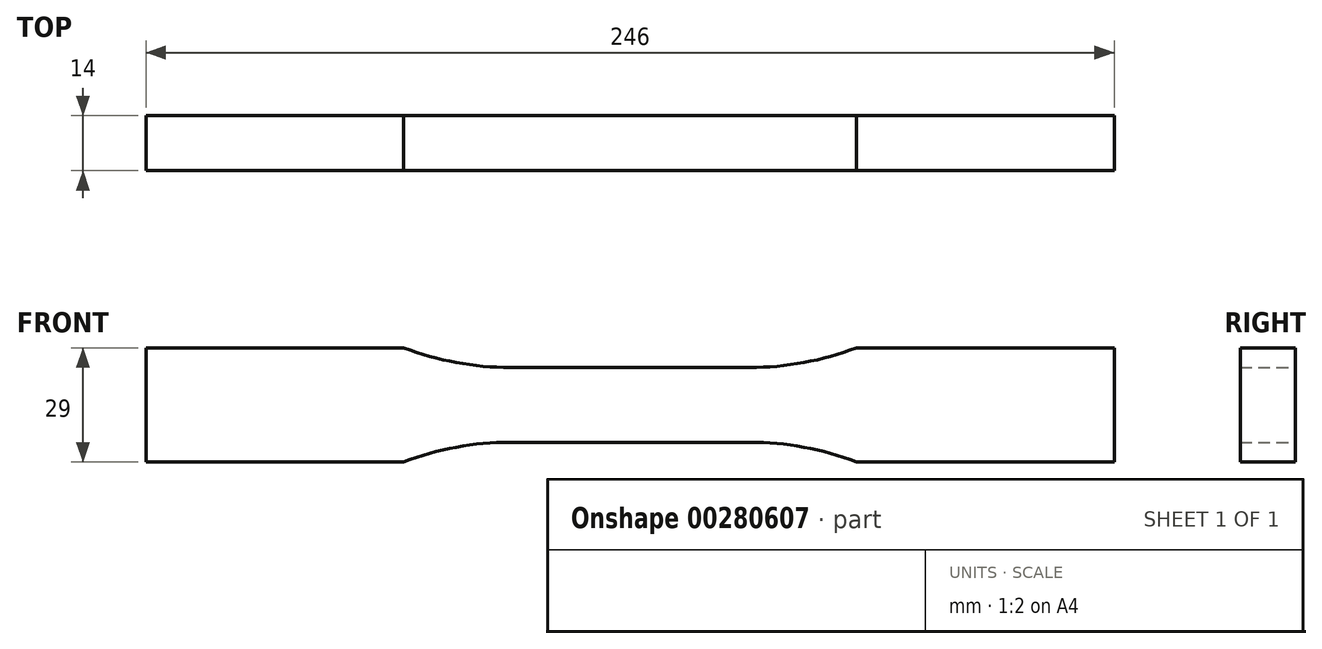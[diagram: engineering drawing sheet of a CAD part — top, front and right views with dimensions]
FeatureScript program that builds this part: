
annotation { "Feature Type Name" : "Feature", "Feature Type Description" : "" }
export const myFeature = defineFeature(function(context is Context, id is Id, definition is map)
    precondition{}
    {
        {
            var Q0;
            Q0=qCreatedBy(makeId("Front.planeOp"),FACE);
            var sketch = newSketch(context, id + "F0", { "sketchPlane" : qUnion([Q0])});
            skLineSegment(sketch, "E0", {"start": v(0, 9.5) * mm, "end": v(30.39, 9.5) * mm});
            skArc(sketch, "E1", {"start": v(30.39, 9.5) * mm, "mid": v(44.17, 10.76) * mm, "end": v(57.5, 14.5) * mm});
            skLineSegment(sketch, "E2", {"start": v(57.5, 14.5) * mm, "end": v(123, 14.5) * mm});
            skLineSegment(sketch, "E3.MirrorCS", {"start": v(57.5, -14.5) * mm, "end": v(123, -14.5) * mm});
            skLineSegment(sketch, "E4.MirrorCS", {"start": v(0, -9.5) * mm, "end": v(30.39, -9.5) * mm});
            skArc(sketch, "E5.MirrorCS", {"start": v(30.39, -9.5) * mm, "mid": v(44.17, -10.76) * mm, "end": v(57.5, -14.5) * mm});
            skArc(sketch, "E6.MirrorCS", {"start": v(-30.39, -9.5) * mm, "mid": v(-44.17, -10.76) * mm, "end": v(-57.5, -14.5) * mm});
            skLineSegment(sketch, "E7.MirrorCS", {"start": v(0, 9.5) * mm, "end": v(-30.39, 9.5) * mm});
            skArc(sketch, "E8.MirrorCS", {"start": v(-30.39, 9.5) * mm, "mid": v(-44.17, 10.76) * mm, "end": v(-57.5, 14.5) * mm});
            skLineSegment(sketch, "E9.MirrorCS", {"start": v(-57.5, -14.5) * mm, "end": v(-123, -14.5) * mm});
            skLineSegment(sketch, "E10.MirrorCS", {"start": v(0, -9.5) * mm, "end": v(-30.39, -9.5) * mm});
            skLineSegment(sketch, "E11.MirrorCS", {"start": v(-57.5, 14.5) * mm, "end": v(-123, 14.5) * mm});
            skLineSegment(sketch, "E12", {"start": v(-123, -14.5) * mm, "end": v(-123, 14.5) * mm});
            skLineSegment(sketch, "E13", {"start": v(123, -14.5) * mm, "end": v(123, 14.5) * mm});
            skSolve(sketch);
        }
        {
            var Q0;
            Q0=makeQuery(id+"F0.imprint","IMPRINT",FACE,{"disambiguationData":[TD([[makeQuery(id+"F0.imprint","IMPRINT",EDGE,{"derivedFrom":sQuery(id+"F0.wireOp",EDGE,"E0")}),-1.0]])]});
            extrude(context, id + "F1", {"entities" : qUnion([Q0]), "endBound" : BoundingType.SYMMETRIC, "depth" : 14 * mm});
        }
    });
